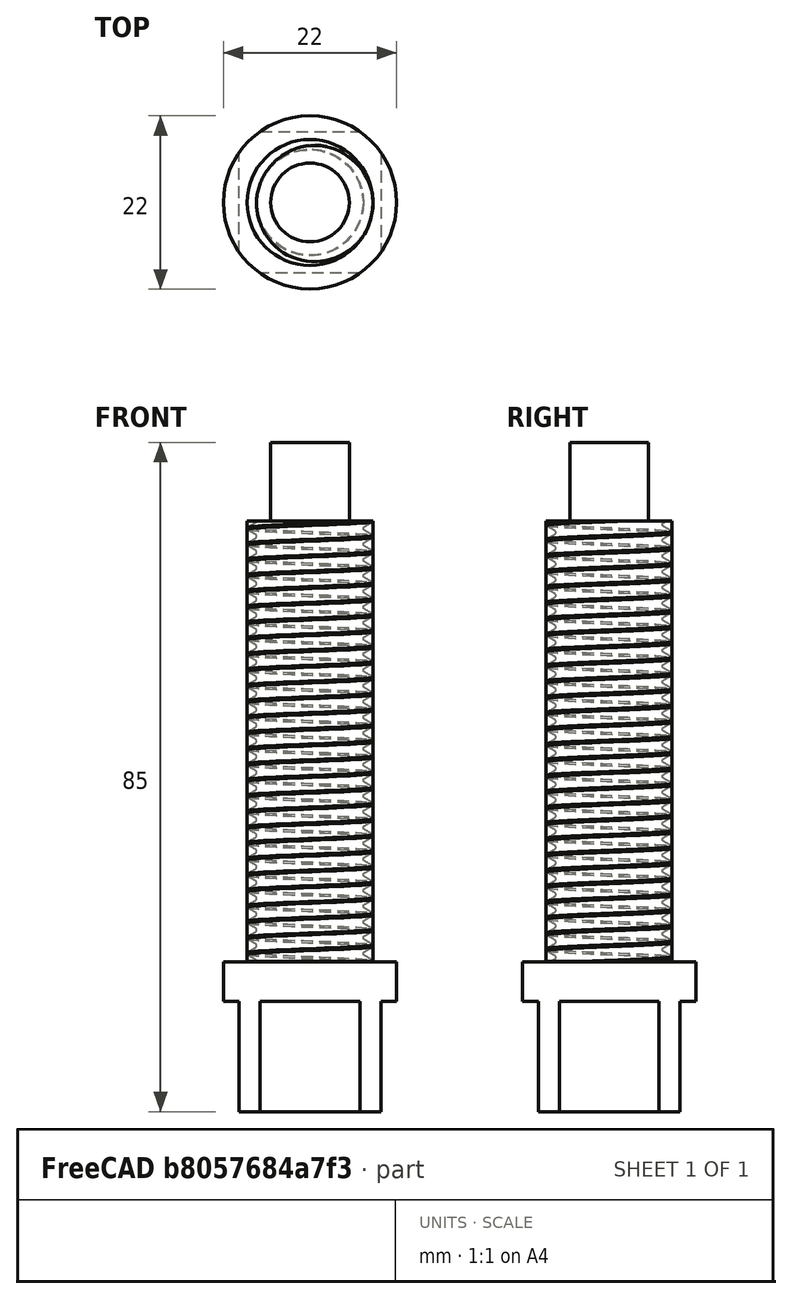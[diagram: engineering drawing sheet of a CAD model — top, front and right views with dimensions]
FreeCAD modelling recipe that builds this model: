
FCSTD DOCUMENT  (FreeCAD 1.0R39109 (Git))
Label: 8-set screw
License: All rights reserved
LicenseURL: https://en.wikipedia.org/wiki/All_rights_reserved
objects: Sketcher::SketchObject×4, PartDesign::Pad×3, Part::Cut×2, PartDesign::Pocket×1, PartDesign::Body×1, Part::FeaturePython×1
note: 24 computed .brp shape members not serialized (recipe doc carries the construction recipe); baked Part::Feature solids carry a one-line shape summary decoded from their .brp

FEATURE [Sketcher::SketchObject] Sketch
  ArcFitTolerance = 1e-06
  AttachmentSupport = -> [XY_Plane]
  FullyConstrained = true
  MakeInternals = false
  MapMode = 5
  sketch-geometry (1):
    g0: Circle CenterX=0 CenterY=0 CenterZ=0 NormalX=0 NormalY=0 NormalZ=1 AngleXU=0 Radius=11
  constraints (2):
    c: Diameter(g0) = 22
    c: Coincident(g0,g-1)
FEATURE [PartDesign::Pad] Pad
  Direction = (0,0,1)
  Length = 19
  Length2 = 10
  Profile = -> Sketch
  ReferenceAxis = -> Sketch [N_Axis]
  Refine = true
  Suppressed = false
  Type = 0
FEATURE [Sketcher::SketchObject] Sketch001
  ArcFitTolerance = 1e-06
  AttachmentSupport = -> [Pad]
  FullyConstrained = false
  MakeInternals = false
  MapMode = 5
  Placement = pos=(0,0,0) rot=(1,0,0;3.14159rad)
  sketch-geometry (6):
    g0: LineSegment StartX=-9 StartY=-9 StartZ=0 EndX=9 EndY=-9 EndZ=0
    g1: LineSegment StartX=9 StartY=-9 StartZ=0 EndX=9 EndY=9 EndZ=0
    g2: LineSegment StartX=9 StartY=9 StartZ=0 EndX=-9 EndY=9 EndZ=0
    g3: LineSegment StartX=-9 StartY=9 StartZ=0 EndX=-9 EndY=-9 EndZ=0
    g4: GeomPoint [constr] X=0 Y=0 Z=0
    g5: Circle CenterX=0 CenterY=0 CenterZ=0 NormalX=0 NormalY=0 NormalZ=1 AngleXU=0 Radius=14.4635
  constraints (13):
    c: Coincident(g0,g1)
    c: Coincident(g1,g2)
    c: Coincident(g2,g3)
    c: Coincident(g3,g0)
    c: Horizontal(g0)
    c: Horizontal(g2)
    c: Vertical(g1)
    c: Vertical(g3)
    c: Symmetric(g2,g0,g4)
    c: Distance(g1,g3) = 18
    c: Distance(g0,g2) = 18
    c: Coincident(g4,g-1)
    c: Coincident(g5,g4)
FEATURE [PartDesign::Pocket] Pocket
  BaseFeature = -> Pad
  Direction = (0,0,1)
  Length = 14
  Length2 = 5
  Profile = -> Sketch001
  ReferenceAxis = -> Sketch001 [N_Axis]
  Refine = true
  Suppressed = false
  Type = 0
FEATURE [Sketcher::SketchObject] Sketch002
  ArcFitTolerance = 1e-06
  AttachmentSupport = -> [Pocket]
  FullyConstrained = true
  MakeInternals = false
  MapMode = 5
  Placement = pos=(0,0,19) rot=(0,0,1;0rad)
  sketch-geometry (1):
    g0: Circle CenterX=0 CenterY=0 CenterZ=0 NormalX=0 NormalY=0 NormalZ=1 AngleXU=0 Radius=8
  constraints (2):
    c: Diameter(g0) = 16
    c: Coincident(g0,g-1)
FEATURE [PartDesign::Pad] Pad001
  BaseFeature = -> Pocket
  Direction = (0,0,1)
  Length = 56
  Length2 = 10
  Profile = -> Sketch002
  ReferenceAxis = -> Sketch002 [N_Axis]
  Refine = true
  Suppressed = false
  Type = 0
FEATURE [Sketcher::SketchObject] Sketch003
  ArcFitTolerance = 1e-06
  AttachmentSupport = -> [Pad001]
  FullyConstrained = true
  MakeInternals = false
  MapMode = 5
  Placement = pos=(0,0,75) rot=(0,0,1;0rad)
  sketch-geometry (1):
    g0: Circle CenterX=0 CenterY=0 CenterZ=0 NormalX=0 NormalY=0 NormalZ=1 AngleXU=0 Radius=5
  constraints (2):
    c: Diameter(g0) = 10
    c: Coincident(g0,g-1)
FEATURE [PartDesign::Body] Body
  AllowCompound = false
  Group = -> [Sketch,Pad,Sketch001,Pocket,Sketch002,Pad001,Sketch003]
  Origin = -> Origin
  Tip = -> Pad001
FEATURE [PartDesign::Pad] Pad002
  BaseFeature = -> Pad001
  Direction = (0,0,1)
  Length = 10
  Length2 = 10
  Profile = -> Sketch003
  ReferenceAxis = -> Sketch003 [N_Axis]
  Refine = true
  Suppressed = false
  Type = 0
FEATURE [Part::FeaturePython] ScrewDie  label="M16x58-Плашка"  # WARN: FeaturePython — macro-defined, semantics opaque (R4)
  Diameter = 13
  DiameterCustom = 16
  Invert = false
  LeftHanded = false
  Length = 58
  MatchOuter = false
  OffsetAngle = 0
  PitchCustom = 1
  Placement = pos=(0,0,77.08) rot=(0,0,1;0rad)
  Thread = true
  Type = 0
FEATURE [Part::Cut] Cut
  Base = -> Pad002
  Refine = true
  Tool = -> ScrewDie
FEATURE [Part::Cut] Cut001
  Base = -> Pad002
  Refine = true
  Tool = -> ScrewDie
